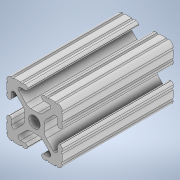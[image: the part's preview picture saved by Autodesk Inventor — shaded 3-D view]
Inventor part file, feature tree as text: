
AUTODESK INVENTOR PART (.ipt)
format: ipt  version: 2020 (Build 240168000, 168)  size: 237,568 bytes
history: native  units: in
note: dims shown in document units (in); Inventor stores cm internally (conversion verified against a paired STEP export)
features: extrude x1, sketch x1
ambient origin geometry x8: Origin, YZ Plane, XZ Plane, XY Plane, X Axis, Y Axis, Z Axis, Center Point
bodies: Solid1 (feature_tree)
feature tree (2):
  extrude  "Extrusion1"  [1 undecoded]
  sketch  "Sketch1"  dims[d0=2.0in d1=0.0in]
note: 1 required parameter value undecoded (feature->parameter linkage not recoverable at this tier; creation-order binding heuristic only, values carry confidence <= 0.55)
